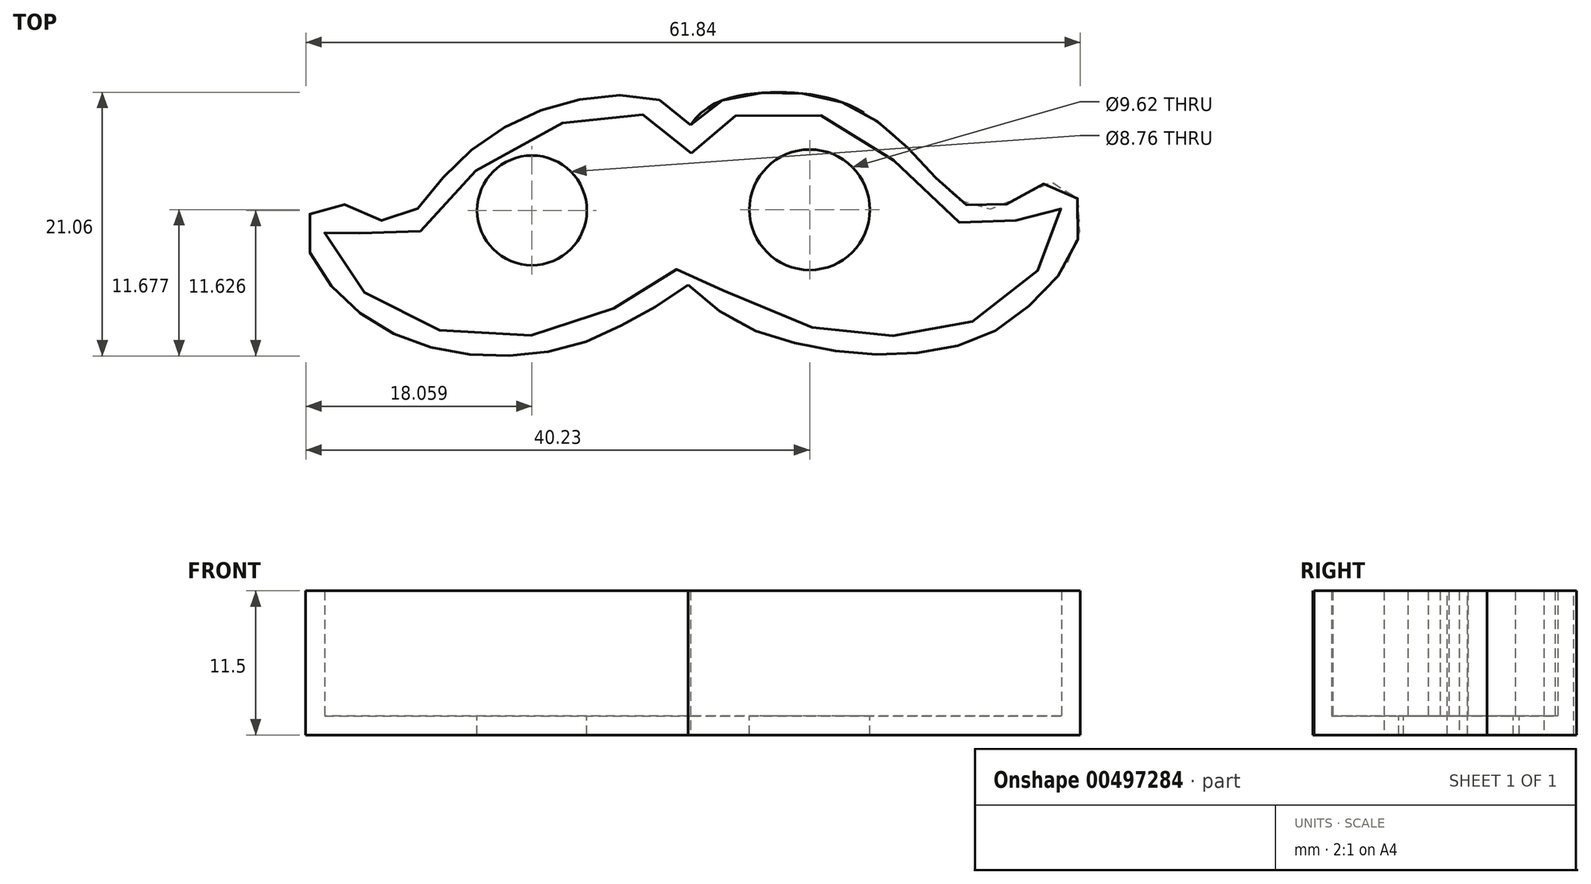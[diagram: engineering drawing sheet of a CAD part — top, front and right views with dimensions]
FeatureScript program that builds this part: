
annotation { "Feature Type Name" : "Feature", "Feature Type Description" : "" }
export const myFeature = defineFeature(function(context is Context, id is Id, definition is map)
    precondition{}
    {
        {
            var Q0;
            Q0=qCreatedBy(makeId("Top.planeOp"),FACE);
            var sketch = newSketch(context, id + "F0", { "sketchPlane" : qUnion([Q0])});
            skFitSpline(sketch, "E0", {"points": [v(-9.47, -5.76) * mm, v(-8.05, -4.02) * mm, v(-4.66, -2.53) * mm, v(1.56, -2.92) * mm, v(6.45, -6.07) * mm, v(11.41, -10.96) * mm, v(14.09, -11.74) * mm, v(16.93, -10.88) * mm, v(19.68, -9.54) * mm, v(20.08, -10.4) * mm, v(19.6, -13.16) * mm, v(15.2, -17.89) * mm, v(11.65, -19.62) * mm, v(5.9, -20.33) * mm, v(0.78, -19.78) * mm, v(-6.08, -17.34) * mm, v(-9.94, -14.34) * mm, v(-10.65, -15.05) * mm, v(-14.04, -17.26) * mm, v(-19.08, -19.62) * mm, v(-25.93, -20.41) * mm, v(-32, -19.07) * mm, v(-36.57, -15.92) * mm, v(-38.7, -12.45) * mm, v(-38.38, -11.11) * mm, v(-36.88, -11.67) * mm, v(-33.81, -12.7) * mm, v(-30.9, -11.82) * mm, v(-27.5, -7.96) * mm, v(-20.89, -3.7) * mm, v(-14.98, -2.6) * mm, v(-11.44, -3.55) * mm, v(-9.47, -5.76) * mm]});
            skSolve(sketch);
        }
        {
            var Q0;
            Q0 = qSketchRegion(id + "F0", true);
            extrude(context, id + "F1", {"entities" : qUnion([Q0]), "depth" : 10 * mm});
        }
        {
            var Q0;
            Q0=makeQuery(id+"F1.opExtrude","CAP_FACE",FACE,{"disambiguationData":[OSD([sQuery(id+"F0.wireOp",EDGE,"E0")])],"isStart":false});
            shell(context, id + "F2", {"entities" : qUnion([Q0]), "thickness" : 1.5 * mm, "oppositeDirection" : true});
        }
        {
            var Q0;
            {var subQ0=sQuery(id+"F0.wireOp",EDGE,"E0");Q0=makeQuery(id+"F2.opShell","OFFSET_FACE",FACE,{"disambiguationData":[OSD([subQ0]),TDD([makeQuery(id+"F1.opExtrude","CAP_FACE",FACE,{"disambiguationData":[OSD([subQ0])],"isStart":true})])]});}
            var sketch = newSketch(context, id + "F3", { "sketchPlane" : qUnion([Q0])});
            skCircle(sketch, "E1", {"center": v(-22.17, -10.31) * mm, "radius": 4.38 * mm});
            skCircle(sketch, "E2", {"center": v(0, -10.26) * mm, "radius": 4.8 * mm});
            skSolve(sketch);
        }
        {
            var Q0;
            Q0 = qSketchRegion(id + "F3", true);
            extrude(context, id + "F4", {"entities" : qUnion([Q0]), "operationType" : NewBodyOperationType.REMOVE, "oppositeDirection" : true, "depth" : 25.4 * mm});
        }
    });
